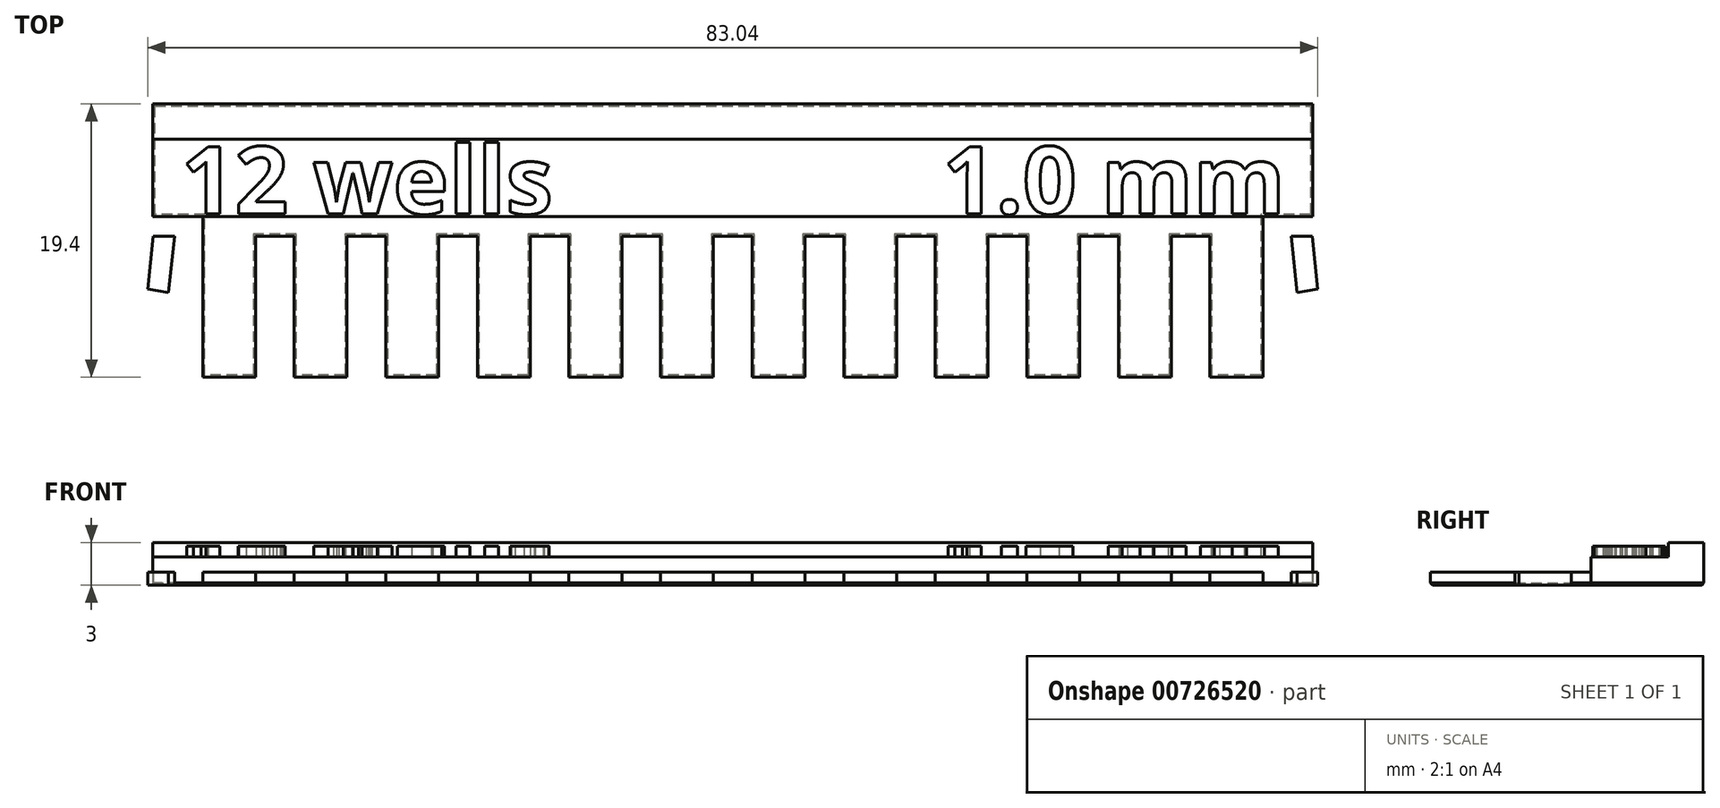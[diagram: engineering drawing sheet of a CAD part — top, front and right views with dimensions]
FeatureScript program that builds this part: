
annotation { "Feature Type Name" : "Feature", "Feature Type Description" : "" }
export const myFeature = defineFeature(function(context is Context, id is Id, definition is map)
    precondition{}
    {
        {
            var Q0;
            Q0=qCreatedBy(makeId("Top.planeOp"),FACE);
            var sketch = newSketch(context, id + "F0", { "sketchPlane" : qUnion([Q0])});
            skLineSegment(sketch, "E0", {"start": v(-46.61, -19.4) * mm, "end": v(-50.36, -19.4) * mm});
            skLineSegment(sketch, "E1", {"start": v(-50.36, -19.4) * mm, "end": v(-50.36, -9.4) * mm});
            skLineSegment(sketch, "E2", {"start": v(-46.61, -9.4) * mm, "end": v(-46.61, -19.4) * mm});
            skLineSegment(sketch, "E3.1.0.0", {"start": v(-43.86, -19.4) * mm, "end": v(-43.86, -9.4) * mm});
            skLineSegment(sketch, "E3.1.0.1", {"start": v(-40.11, -19.4) * mm, "end": v(-43.86, -19.4) * mm});
            skLineSegment(sketch, "E3.1.0.2", {"start": v(-40.11, -9.4) * mm, "end": v(-40.11, -19.4) * mm});
            skLineSegment(sketch, "E3.2.0.0", {"start": v(-37.36, -19.4) * mm, "end": v(-37.36, -9.4) * mm});
            skLineSegment(sketch, "E3.2.0.1", {"start": v(-33.61, -19.4) * mm, "end": v(-37.36, -19.4) * mm});
            skLineSegment(sketch, "E3.2.0.2", {"start": v(-33.61, -9.4) * mm, "end": v(-33.61, -19.4) * mm});
            skLineSegment(sketch, "E3.3.0.0", {"start": v(-30.86, -19.4) * mm, "end": v(-30.86, -9.4) * mm});
            skLineSegment(sketch, "E3.3.0.1", {"start": v(-27.11, -19.4) * mm, "end": v(-30.86, -19.4) * mm});
            skLineSegment(sketch, "E3.3.0.2", {"start": v(-27.11, -9.4) * mm, "end": v(-27.11, -19.4) * mm});
            skLineSegment(sketch, "E3.4.0.0", {"start": v(-24.36, -19.4) * mm, "end": v(-24.36, -9.4) * mm});
            skLineSegment(sketch, "E3.4.0.1", {"start": v(-20.61, -19.4) * mm, "end": v(-24.36, -19.4) * mm});
            skLineSegment(sketch, "E3.4.0.2", {"start": v(-20.61, -9.4) * mm, "end": v(-20.61, -19.4) * mm});
            skLineSegment(sketch, "E3.5.0.0", {"start": v(-17.86, -19.4) * mm, "end": v(-17.86, -9.4) * mm});
            skLineSegment(sketch, "E3.5.0.1", {"start": v(-14.11, -19.4) * mm, "end": v(-17.86, -19.4) * mm});
            skLineSegment(sketch, "E3.5.0.2", {"start": v(-14.11, -9.4) * mm, "end": v(-14.11, -19.4) * mm});
            skLineSegment(sketch, "E3.6.0.0", {"start": v(-11.36, -19.4) * mm, "end": v(-11.36, -9.4) * mm});
            skLineSegment(sketch, "E3.6.0.1", {"start": v(-7.61, -19.4) * mm, "end": v(-11.36, -19.4) * mm});
            skLineSegment(sketch, "E3.6.0.2", {"start": v(-7.61, -9.4) * mm, "end": v(-7.61, -19.4) * mm});
            skLineSegment(sketch, "E3.7.0.0", {"start": v(-4.86, -19.4) * mm, "end": v(-4.86, -9.4) * mm});
            skLineSegment(sketch, "E3.7.0.1", {"start": v(-1.11, -19.4) * mm, "end": v(-4.86, -19.4) * mm});
            skLineSegment(sketch, "E3.7.0.2", {"start": v(-1.11, -9.4) * mm, "end": v(-1.11, -19.4) * mm});
            skLineSegment(sketch, "E3.8.0.0", {"start": v(1.64, -19.4) * mm, "end": v(1.64, -9.4) * mm});
            skLineSegment(sketch, "E3.8.0.1", {"start": v(5.39, -19.4) * mm, "end": v(1.64, -19.4) * mm});
            skLineSegment(sketch, "E3.8.0.2", {"start": v(5.39, -9.4) * mm, "end": v(5.39, -19.4) * mm});
            skLineSegment(sketch, "E3.9.0.0", {"start": v(8.14, -19.4) * mm, "end": v(8.14, -9.4) * mm});
            skLineSegment(sketch, "E3.9.0.1", {"start": v(11.89, -19.4) * mm, "end": v(8.14, -19.4) * mm});
            skLineSegment(sketch, "E3.9.0.2", {"start": v(11.89, -9.4) * mm, "end": v(11.89, -19.4) * mm});
            skLineSegment(sketch, "E3.10.0.0", {"start": v(14.64, -19.4) * mm, "end": v(14.64, -9.4) * mm});
            skLineSegment(sketch, "E3.10.0.1", {"start": v(18.39, -19.4) * mm, "end": v(14.64, -19.4) * mm});
            skLineSegment(sketch, "E3.10.0.2", {"start": v(18.39, -9.4) * mm, "end": v(18.39, -19.4) * mm});
            skLineSegment(sketch, "E3.11.0.0", {"start": v(21.14, -19.4) * mm, "end": v(21.14, -9.4) * mm});
            skLineSegment(sketch, "E3.11.0.1", {"start": v(24.89, -19.4) * mm, "end": v(21.14, -19.4) * mm});
            skLineSegment(sketch, "E3.11.0.2", {"start": v(24.89, -9.4) * mm, "end": v(24.89, -19.4) * mm});
            skLineSegment(sketch, "E3.direction1", {"start": v(-50.36, -19.4) * mm, "end": v(-43.86, -19.4) * mm, "construction": true});
            skLineSegment(sketch, "E4", {"start": v(-53.87, -9.4) * mm, "end": v(28.37, -9.4) * mm});
            skLineSegment(sketch, "E5", {"start": v(-50.36, -9.4) * mm, "end": v(-50.36, -8) * mm});
            skLineSegment(sketch, "E6", {"start": v(-53.89, -8) * mm, "end": v(28.41, -8) * mm});
            skLineSegment(sketch, "E7", {"start": v(-50.36, -8) * mm, "end": v(-53.89, -8) * mm});
            skLineSegment(sketch, "E8", {"start": v(24.89, -8) * mm, "end": v(28.41, -8) * mm});
            skLineSegment(sketch, "E9", {"start": v(-53.89, -8) * mm, "end": v(-53.89, -9.22) * mm});
            skLineSegment(sketch, "E10", {"start": v(-53.89, -9.22) * mm, "end": v(-53.89, -9.4) * mm, "construction": true});
            skLineSegment(sketch, "E11", {"start": v(-53.87, -9.4) * mm, "end": v(-53.89, -9.4) * mm, "construction": true});
            skLineSegment(sketch, "E12", {"start": v(-53.87, -9.4) * mm, "end": v(-54.26, -13.13) * mm});
            skLineSegment(sketch, "E13", {"start": v(-54.26, -13.13) * mm, "end": v(-52.78, -13.4) * mm});
            skLineSegment(sketch, "E14", {"start": v(-52.78, -13.4) * mm, "end": v(-52.36, -9.4) * mm});
            skLineSegment(sketch, "E15", {"start": v(-53.87, -9.4) * mm, "end": v(-53.85, -9.22) * mm});
            skLineSegment(sketch, "E16", {"start": v(-53.89, -9.22) * mm, "end": v(-53.85, -9.22) * mm});
            skLineSegment(sketch, "E17", {"start": v(-46.61, -9.4) * mm, "end": v(24.89, -9.4) * mm});
            skLineSegment(sketch, "E18", {"start": v(-12.74, 1.4) * mm, "end": v(-12.74, -28.66) * mm, "construction": true});
            skLineSegment(sketch, "E19.MirrorCS", {"start": v(24.89, -9.4) * mm, "end": v(24.89, -8) * mm});
            skLineSegment(sketch, "E20.MirrorCS", {"start": v(28.41, -8) * mm, "end": v(28.41, -9.22) * mm});
            skLineSegment(sketch, "E21.MirrorCS", {"start": v(28.41, -9.22) * mm, "end": v(28.37, -9.22) * mm});
            skLineSegment(sketch, "E22.MirrorCS", {"start": v(28.39, -9.4) * mm, "end": v(28.37, -9.22) * mm});
            skLineSegment(sketch, "E23.MirrorCS", {"start": v(28.39, -9.4) * mm, "end": v(-53.85, -9.4) * mm});
            skLineSegment(sketch, "E24.MirrorCS", {"start": v(28.39, -9.4) * mm, "end": v(28.78, -13.13) * mm});
            skLineSegment(sketch, "E25.MirrorCS", {"start": v(28.78, -13.13) * mm, "end": v(27.3, -13.4) * mm});
            skLineSegment(sketch, "E26.MirrorCS", {"start": v(27.3, -13.4) * mm, "end": v(26.89, -9.4) * mm});
            skLineSegment(sketch, "E27.MirrorCS", {"start": v(24.89, -19.4) * mm, "end": v(24.89, -9.4) * mm});
            skLineSegment(sketch, "E28", {"start": v(28.41, -8) * mm, "end": v(28.41, -2.5) * mm});
            skLineSegment(sketch, "E29", {"start": v(28.41, -2.5) * mm, "end": v(-53.89, -2.5) * mm});
            skLineSegment(sketch, "E30", {"start": v(-53.89, -2.5) * mm, "end": v(-53.89, -8) * mm});
            skLineSegment(sketch, "E31", {"start": v(28.41, -2.5) * mm, "end": v(28.41, 0) * mm});
            skLineSegment(sketch, "E32", {"start": v(28.41, 0) * mm, "end": v(-53.89, 0) * mm});
            skLineSegment(sketch, "E33", {"start": v(-53.89, 0) * mm, "end": v(-53.89, -2.5) * mm});
            skSolve(sketch);
        }
        {
            var Q0;
            {var subQ1=sQuery(id+"F0.wireOp",EDGE,"E4");Q0=makeQuery(id+"F0.imprint","IMPRINT",FACE,{"disambiguationData":[TD([[makeQuery(id+"F0.imprint","IMPRINT",EDGE,{"derivedFrom":subQ1}),-1.0]])]});}
            var Q1;
            {var subQ1=sQuery(id+"F0.wireOp",EDGE,"E4");Q1=makeQuery(id+"F0.imprint","IMPRINT",FACE,{"disambiguationData":[TD([[makeQuery(id+"F0.imprint","IMPRINT",EDGE,{"derivedFrom":subQ1}),1.0]])]});}
            var Q2;
            {var subQ19=sQuery(id+"F0.wireOp",EDGE,"E5");Q2=makeQuery(id+"F0.imprint","IMPRINT",FACE,{"disambiguationData":[TD([[makeQuery(id+"F0.imprint","IMPRINT",EDGE,{"derivedFrom":subQ19}),-1.0]])]});}
            var Q3;
            Q3=makeQuery(id+"F0.imprint","IMPRINT",FACE,{"disambiguationData":[TD([[makeQuery(id+"F0.imprint","IMPRINT",EDGE,{"derivedFrom":sQuery(id+"F0.wireOp",EDGE,"E0")}),-1.0]])]});
            var Q4;
            {var subQ0=sQuery(id+"F0.wireOp",EDGE,"E3.1.0.0");Q4=makeQuery(id+"F0.imprint","IMPRINT",FACE,{"disambiguationData":[TD([[makeQuery(id+"F0.imprint","IMPRINT",EDGE,{"derivedFrom":subQ0}),-1.0]])]});}
            var Q5;
            {var subQ0=sQuery(id+"F0.wireOp",EDGE,"E3.2.0.0");Q5=makeQuery(id+"F0.imprint","IMPRINT",FACE,{"disambiguationData":[TD([[makeQuery(id+"F0.imprint","IMPRINT",EDGE,{"derivedFrom":subQ0}),-1.0]])]});}
            var Q6;
            {var subQ0=sQuery(id+"F0.wireOp",EDGE,"E3.3.0.0");Q6=makeQuery(id+"F0.imprint","IMPRINT",FACE,{"disambiguationData":[TD([[makeQuery(id+"F0.imprint","IMPRINT",EDGE,{"derivedFrom":subQ0}),-1.0]])]});}
            var Q7;
            {var subQ0=sQuery(id+"F0.wireOp",EDGE,"E3.4.0.0");Q7=makeQuery(id+"F0.imprint","IMPRINT",FACE,{"disambiguationData":[TD([[makeQuery(id+"F0.imprint","IMPRINT",EDGE,{"derivedFrom":subQ0}),-1.0]])]});}
            var Q8;
            {var subQ0=sQuery(id+"F0.wireOp",EDGE,"E3.5.0.0");Q8=makeQuery(id+"F0.imprint","IMPRINT",FACE,{"disambiguationData":[TD([[makeQuery(id+"F0.imprint","IMPRINT",EDGE,{"derivedFrom":subQ0}),-1.0]])]});}
            var Q9;
            {var subQ0=sQuery(id+"F0.wireOp",EDGE,"E3.6.0.0");Q9=makeQuery(id+"F0.imprint","IMPRINT",FACE,{"disambiguationData":[TD([[makeQuery(id+"F0.imprint","IMPRINT",EDGE,{"derivedFrom":subQ0}),-1.0]])]});}
            var Q10;
            {var subQ0=sQuery(id+"F0.wireOp",EDGE,"E3.7.0.0");Q10=makeQuery(id+"F0.imprint","IMPRINT",FACE,{"disambiguationData":[TD([[makeQuery(id+"F0.imprint","IMPRINT",EDGE,{"derivedFrom":subQ0}),-1.0]])]});}
            var Q11;
            {var subQ0=sQuery(id+"F0.wireOp",EDGE,"E3.8.0.0");Q11=makeQuery(id+"F0.imprint","IMPRINT",FACE,{"disambiguationData":[TD([[makeQuery(id+"F0.imprint","IMPRINT",EDGE,{"derivedFrom":subQ0}),-1.0]])]});}
            var Q12;
            {var subQ0=sQuery(id+"F0.wireOp",EDGE,"E3.9.0.0");Q12=makeQuery(id+"F0.imprint","IMPRINT",FACE,{"disambiguationData":[TD([[makeQuery(id+"F0.imprint","IMPRINT",EDGE,{"derivedFrom":subQ0}),-1.0]])]});}
            var Q13;
            {var subQ0=sQuery(id+"F0.wireOp",EDGE,"E3.10.0.0");Q13=makeQuery(id+"F0.imprint","IMPRINT",FACE,{"disambiguationData":[TD([[makeQuery(id+"F0.imprint","IMPRINT",EDGE,{"derivedFrom":subQ0}),-1.0]])]});}
            var Q14;
            {var subQ0=sQuery(id+"F0.wireOp",EDGE,"E3.11.0.0");Q14=makeQuery(id+"F0.imprint","IMPRINT",FACE,{"disambiguationData":[TD([[makeQuery(id+"F0.imprint","IMPRINT",EDGE,{"derivedFrom":subQ0}),-1.0]])]});}
            var Q15;
            Q15=makeQuery(id+"F0.imprint","IMPRINT",FACE,{"disambiguationData":[TD([[makeQuery(id+"F0.imprint","IMPRINT",EDGE,{"derivedFrom":sQuery(id+"F0.wireOp",EDGE,"E8")}),-1.0]])]});
            var Q16;
            {var subQ0=sQuery(id+"F0.wireOp",EDGE,"E24.MirrorCS");Q16=makeQuery(id+"F0.imprint","IMPRINT",FACE,{"disambiguationData":[TD([[makeQuery(id+"F0.imprint","IMPRINT",EDGE,{"derivedFrom":subQ0}),-1.0]])]});}
            extrude(context, id + "F1", {"entities" : qUnion([Q0, Q1, Q2, Q3, Q4, Q5, Q6, Q7, Q8, Q9, Q10, Q11, Q12, Q13, Q14, Q15, Q16]), "depth" : 0.9 * mm, "offsetDistance" : 25 * mm});
        }
        {
            var Q0;
            Q0=makeQuery(id+"F0.imprint","IMPRINT",FACE,{"disambiguationData":[TD([[makeQuery(id+"F0.imprint","IMPRINT",EDGE,{"derivedFrom":sQuery(id+"F0.wireOp",EDGE,"E6")}),1.0]])]});
            extrude(context, id + "F2", {"entities" : qUnion([Q0]), "operationType" : NewBodyOperationType.ADD, "depth" : 2 * mm, "offsetDistance" : 25 * mm});
        }
        {
            var Q0;
            Q0=makeQuery(id+"F0.imprint","IMPRINT",FACE,{"disambiguationData":[TD([[makeQuery(id+"F0.imprint","IMPRINT",EDGE,{"derivedFrom":sQuery(id+"F0.wireOp",EDGE,"E29")}),-1.0]])]});
            extrude(context, id + "F3", {"entities" : qUnion([Q0]), "operationType" : NewBodyOperationType.ADD, "depth" : 3 * mm, "offsetDistance" : 25 * mm});
        }
        {
            var Q0;
            Q0=makeQuery(id+"F2.opExtrude","CAP_FACE",FACE,{"disambiguationData":[OSD([sQuery(id+"F0.wireOp",EDGE,"E6"),sQuery(id+"F0.wireOp",EDGE,"E7"),sQuery(id+"F0.wireOp",EDGE,"E8"),sQuery(id+"F0.wireOp",EDGE,"E28"),sQuery(id+"F0.wireOp",EDGE,"E29"),sQuery(id+"F0.wireOp",EDGE,"E30")])],"isStart":false});
            var sketch = newSketch(context, id + "F4", { "sketchPlane" : qUnion([Q0])});
            skLineSegment(sketch, "E34", {"start": v(-51.89, -2.5) * mm, "end": v(-51.89, -8) * mm, "construction": true});
            skPoint(sketch, "E35", {"position": v(-51.89, -3) * mm});
            skPoint(sketch, "E36", {"position": v(-51.89, -7.8) * mm});
            skText(sketch, "E37", { "text": "12 wells", "fontName": "OpenSans-Bold.ttf"});
            skLineSegment(sketch, "E38", {"start": v(26.41, -2.5) * mm, "end": v(26.41, -8) * mm, "construction": true});
            skPoint(sketch, "E39", {"position": v(26.41, -3) * mm});
            skPoint(sketch, "E40", {"position": v(26.41, -7.8) * mm});
            skText(sketch, "E41", { "text": "1.0 mm", "fontName": "OpenSans-Bold.ttf"});
            const initialGuessF4  = {"E37": [-0.05189, -0.0078, 1, 0, 0.0048], "E41": [0.00214, -0.0078, 1, 0, 0.0048]};
            skSetInitialGuess(sketch, initialGuessF4);
            skSolve(sketch);
        }
        {
            var Q0;
            Q0=makeQuery(id+"F4.imprint","IMPRINT",FACE,{"disambiguationData":[TD([[makeQuery(id+"F4.imprint","IMPRINT",EDGE,{"derivedFrom":sQuery(id+"F4.wireOp",EDGE,"E37.sketch_text.stroke-0")}),-1.0]])]});
            var Q1;
            Q1=makeQuery(id+"F4.imprint","IMPRINT",FACE,{"disambiguationData":[TD([[makeQuery(id+"F4.imprint","IMPRINT",EDGE,{"derivedFrom":sQuery(id+"F4.wireOp",EDGE,"E37.sketch_text.stroke-10")}),-1.0]])]});
            var Q2;
            Q2=makeQuery(id+"F4.imprint","IMPRINT",FACE,{"disambiguationData":[TD([[makeQuery(id+"F4.imprint","IMPRINT",EDGE,{"derivedFrom":sQuery(id+"F4.wireOp",EDGE,"E37.sketch_text.stroke-34")}),-1.0]])]});
            var Q3;
            Q3=makeQuery(id+"F4.imprint","IMPRINT",FACE,{"disambiguationData":[TD([[makeQuery(id+"F4.imprint","IMPRINT",EDGE,{"derivedFrom":sQuery(id+"F4.wireOp",EDGE,"E37.sketch_text.stroke-60")}),-1.0]])]});
            var Q4;
            Q4=makeQuery(id+"F4.imprint","IMPRINT",FACE,{"disambiguationData":[TD([[makeQuery(id+"F4.imprint","IMPRINT",EDGE,{"derivedFrom":sQuery(id+"F4.wireOp",EDGE,"E37.sketch_text.stroke-80")}),-1.0]])]});
            var Q5;
            Q5=makeQuery(id+"F4.imprint","IMPRINT",FACE,{"disambiguationData":[TD([[makeQuery(id+"F4.imprint","IMPRINT",EDGE,{"derivedFrom":sQuery(id+"F4.wireOp",EDGE,"E37.sketch_text.stroke-84")}),-1.0]])]});
            var Q6;
            Q6=makeQuery(id+"F4.imprint","IMPRINT",FACE,{"disambiguationData":[TD([[makeQuery(id+"F4.imprint","IMPRINT",EDGE,{"derivedFrom":sQuery(id+"F4.wireOp",EDGE,"E37.sketch_text.stroke-88")}),-1.0]])]});
            var Q7;
            Q7=makeQuery(id+"F4.imprint","IMPRINT",FACE,{"disambiguationData":[TD([[makeQuery(id+"F4.imprint","IMPRINT",EDGE,{"derivedFrom":sQuery(id+"F4.wireOp",EDGE,"E41.sketch_text.stroke-0")}),-1.0]])]});
            var Q8;
            Q8=makeQuery(id+"F4.imprint","IMPRINT",FACE,{"disambiguationData":[TD([[makeQuery(id+"F4.imprint","IMPRINT",EDGE,{"derivedFrom":sQuery(id+"F4.wireOp",EDGE,"E41.sketch_text.stroke-10")}),-1.0]])]});
            var Q9;
            Q9=makeQuery(id+"F4.imprint","IMPRINT",FACE,{"disambiguationData":[TD([[makeQuery(id+"F4.imprint","IMPRINT",EDGE,{"derivedFrom":sQuery(id+"F4.wireOp",EDGE,"E41.sketch_text.stroke-18")}),-1.0]])]});
            var Q10;
            Q10=makeQuery(id+"F4.imprint","IMPRINT",FACE,{"disambiguationData":[TD([[makeQuery(id+"F4.imprint","IMPRINT",EDGE,{"derivedFrom":sQuery(id+"F4.wireOp",EDGE,"E41.sketch_text.stroke-34")}),-1.0]])]});
            var Q11;
            Q11=makeQuery(id+"F4.imprint","IMPRINT",FACE,{"disambiguationData":[TD([[makeQuery(id+"F4.imprint","IMPRINT",EDGE,{"derivedFrom":sQuery(id+"F4.wireOp",EDGE,"E41.sketch_text.stroke-62")}),-1.0]])]});
            extrude(context, id + "F5", {"entities" : qUnion([Q0, Q1, Q2, Q3, Q4, Q5, Q6, Q7, Q8, Q9, Q10, Q11]), "operationType" : NewBodyOperationType.ADD, "depth" : 0.75 * mm, "offsetDistance" : 25 * mm});
        }
        {
            var Q0;
            {var subQ0=sQuery(id+"F0.wireOp",EDGE,"E29");var subQ1=sQuery(id+"F0.wireOp",EDGE,"E8");var subQ2=sQuery(id+"F0.wireOp",EDGE,"E7");var subQ3=sQuery(id+"F0.wireOp",EDGE,"E6");Q0=makeQuery(id+"F3.boolean.opBoolean","MERGE",FACE,{"derivedFrom":[makeQuery(id+"F2.boolean.opBoolean","MERGE",FACE,{"derivedFrom":[makeQuery(id+"F1.opExtrude","CAP_FACE",FACE,{"disambiguationData":[OSD([sQuery(id+"F0.wireOp",EDGE,"E0"),sQuery(id+"F0.wireOp",EDGE,"E1"),sQuery(id+"F0.wireOp",EDGE,"E2"),sQuery(id+"F0.wireOp",EDGE,"E3.1.0.0"),sQuery(id+"F0.wireOp",EDGE,"E3.1.0.1"),sQuery(id+"F0.wireOp",EDGE,"E3.1.0.2"),sQuery(id+"F0.wireOp",EDGE,"E3.2.0.0"),sQuery(id+"F0.wireOp",EDGE,"E3.2.0.1"),sQuery(id+"F0.wireOp",EDGE,"E3.2.0.2"),sQuery(id+"F0.wireOp",EDGE,"E3.3.0.0"),sQuery(id+"F0.wireOp",EDGE,"E3.3.0.1"),sQuery(id+"F0.wireOp",EDGE,"E3.3.0.2"),sQuery(id+"F0.wireOp",EDGE,"E3.4.0.0"),sQuery(id+"F0.wireOp",EDGE,"E3.4.0.1"),sQuery(id+"F0.wireOp",EDGE,"E3.4.0.2"),sQuery(id+"F0.wireOp",EDGE,"E3.5.0.0"),sQuery(id+"F0.wireOp",EDGE,"E3.5.0.1"),sQuery(id+"F0.wireOp",EDGE,"E3.5.0.2"),sQuery(id+"F0.wireOp",EDGE,"E3.6.0.0"),sQuery(id+"F0.wireOp",EDGE,"E3.6.0.1"),sQuery(id+"F0.wireOp",EDGE,"E3.6.0.2"),sQuery(id+"F0.wireOp",EDGE,"E3.7.0.0"),sQuery(id+"F0.wireOp",EDGE,"E3.7.0.1"),sQuery(id+"F0.wireOp",EDGE,"E3.7.0.2"),sQuery(id+"F0.wireOp",EDGE,"E3.8.0.0"),sQuery(id+"F0.wireOp",EDGE,"E3.8.0.1"),sQuery(id+"F0.wireOp",EDGE,"E3.8.0.2"),sQuery(id+"F0.wireOp",EDGE,"E3.9.0.0"),sQuery(id+"F0.wireOp",EDGE,"E3.9.0.1"),sQuery(id+"F0.wireOp",EDGE,"E3.9.0.2"),sQuery(id+"F0.wireOp",EDGE,"E3.10.0.0"),sQuery(id+"F0.wireOp",EDGE,"E3.10.0.1"),sQuery(id+"F0.wireOp",EDGE,"E3.10.0.2"),sQuery(id+"F0.wireOp",EDGE,"E3.11.0.0"),sQuery(id+"F0.wireOp",EDGE,"E3.11.0.1"),subQ3,subQ2,sQuery(id+"F0.wireOp",EDGE,"E9"),sQuery(id+"F0.wireOp",EDGE,"E12"),sQuery(id+"F0.wireOp",EDGE,"E13"),sQuery(id+"F0.wireOp",EDGE,"E14"),sQuery(id+"F0.wireOp",EDGE,"E15"),sQuery(id+"F0.wireOp",EDGE,"E16"),subQ1,sQuery(id+"F0.wireOp",EDGE,"E20.MirrorCS"),sQuery(id+"F0.wireOp",EDGE,"E21.MirrorCS"),sQuery(id+"F0.wireOp",EDGE,"E22.MirrorCS"),sQuery(id+"F0.wireOp",EDGE,"E23.MirrorCS"),sQuery(id+"F0.wireOp",EDGE,"E24.MirrorCS"),sQuery(id+"F0.wireOp",EDGE,"E25.MirrorCS"),sQuery(id+"F0.wireOp",EDGE,"E26.MirrorCS"),sQuery(id+"F0.wireOp",EDGE,"E27.MirrorCS")])],"isStart":true}),makeQuery(id+"F2.opExtrude","CAP_FACE",FACE,{"disambiguationData":[OSD([subQ3,subQ2,subQ1,sQuery(id+"F0.wireOp",EDGE,"E28"),subQ0,sQuery(id+"F0.wireOp",EDGE,"E30")])],"isStart":true})]}),makeQuery(id+"F3.opExtrude","CAP_FACE",FACE,{"disambiguationData":[OSD([subQ0,sQuery(id+"F0.wireOp",EDGE,"E31"),sQuery(id+"F0.wireOp",EDGE,"E32"),sQuery(id+"F0.wireOp",EDGE,"E33")])],"isStart":true})]});}
            chamfer(context, id + "F6", {"entities" : qUnion([Q0]), "width" : 0.15 * mm, "tangentPropagation" : true});
        }
    });
